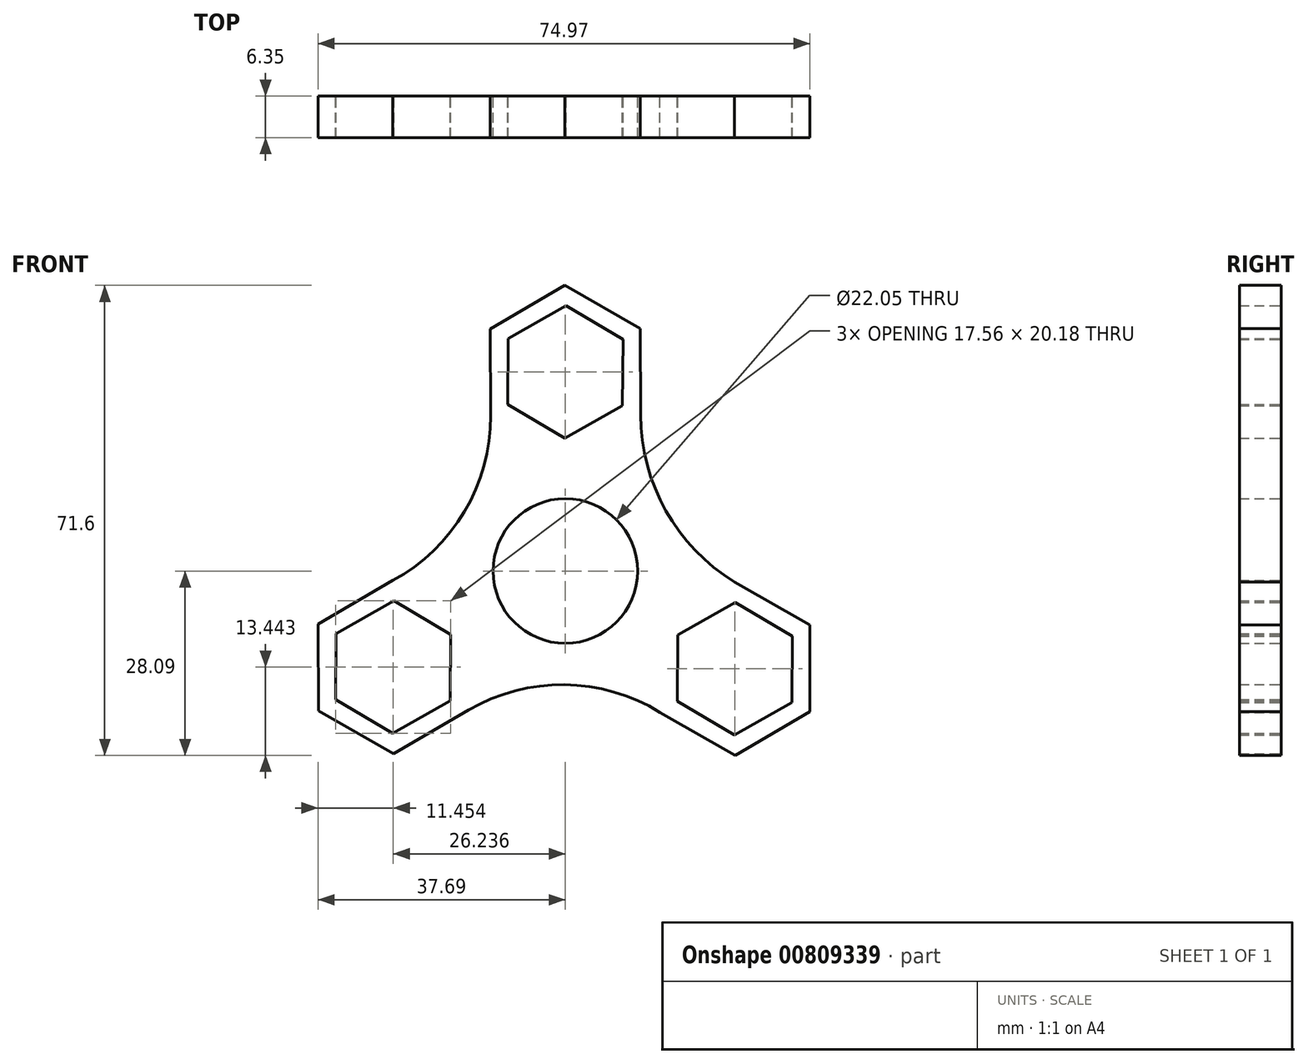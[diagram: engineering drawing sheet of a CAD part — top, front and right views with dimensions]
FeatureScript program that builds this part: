
annotation { "Feature Type Name" : "Feature", "Feature Type Description" : "" }
export const myFeature = defineFeature(function(context is Context, id is Id, definition is map)
    precondition{}
    {
        {
            var Q0;
            Q0=qCreatedBy(makeId("Front.planeOp"),FACE);
            var sketch = newSketch(context, id + "F0", { "sketchPlane" : qUnion([Q0])});
            skCircle(sketch, "E0", {"center": v(0, 0) * mm, "radius": 14.29 * mm});
            skCircle(sketch, "E1", {"center": v(0, 0) * mm, "radius": 11.02 * mm});
            skCircle(sketch, "E2.cCircle", {"center": v(0, 30.31) * mm, "radius": 11.43 * mm, "construction": true});
            skLineSegment(sketch, "E2.0", {"start": v(-0.05, 43.51) * mm, "end": v(11.4, 36.96) * mm});
            skLineSegment(sketch, "E2.1", {"start": v(11.4, 36.96) * mm, "end": v(11.46, 23.76) * mm});
            skLineSegment(sketch, "E2.2", {"start": v(11.46, 23.76) * mm, "end": v(0.05, 17.12) * mm});
            skLineSegment(sketch, "E2.3", {"start": v(0.05, 17.12) * mm, "end": v(-11.4, 23.67) * mm});
            skLineSegment(sketch, "E2.4", {"start": v(-11.4, 23.67) * mm, "end": v(-11.46, 36.87) * mm});
            skLineSegment(sketch, "E2.5", {"start": v(-11.46, 36.87) * mm, "end": v(-0.05, 43.51) * mm});
            skPoint(sketch, "E2.0.midPoint", {"position": v(5.67, 40.24) * mm});
            skCircle(sketch, "E3.cCircle", {"center": v(0, 30.31) * mm, "radius": 8.74 * mm, "construction": true});
            skLineSegment(sketch, "E3.0", {"start": v(0.09, 40.4) * mm, "end": v(8.78, 35.28) * mm});
            skLineSegment(sketch, "E3.1", {"start": v(8.78, 35.28) * mm, "end": v(8.7, 25.2) * mm});
            skLineSegment(sketch, "E3.2", {"start": v(8.7, 25.2) * mm, "end": v(-0.09, 20.22) * mm});
            skLineSegment(sketch, "E3.3", {"start": v(-0.09, 20.22) * mm, "end": v(-8.78, 25.35) * mm});
            skLineSegment(sketch, "E3.4", {"start": v(-8.78, 25.35) * mm, "end": v(-8.7, 35.44) * mm});
            skLineSegment(sketch, "E3.5", {"start": v(-8.7, 35.44) * mm, "end": v(0.09, 40.4) * mm});
            skPoint(sketch, "E3.0.midPoint", {"position": v(4.44, 37.84) * mm});
            skLineSegment(sketch, "E4.1.0", {"start": v(-14.83, -8) * mm, "end": v(-14.78, -21.2) * mm});
            skLineSegment(sketch, "E4.1.1", {"start": v(-26.29, -1.45) * mm, "end": v(-14.83, -8) * mm});
            skLineSegment(sketch, "E4.1.2", {"start": v(-14.78, -21.2) * mm, "end": v(-26.18, -27.84) * mm});
            skPoint(sketch, "E4.1.3", {"position": v(-34.97, -14.57) * mm});
            skLineSegment(sketch, "E4.1.4", {"start": v(-26.18, -27.84) * mm, "end": v(-37.64, -21.3) * mm});
            skLineSegment(sketch, "E4.1.5", {"start": v(-37.7, -8.1) * mm, "end": v(-26.29, -1.45) * mm});
            skLineSegment(sketch, "E4.1.6", {"start": v(-17.54, -19.77) * mm, "end": v(-26.33, -24.74) * mm});
            skLineSegment(sketch, "E4.1.7", {"start": v(-26.33, -24.74) * mm, "end": v(-35.02, -19.61) * mm});
            skPoint(sketch, "E4.1.9", {"position": v(-37.67, -14.7) * mm});
            skLineSegment(sketch, "E4.1.10", {"start": v(-26.15, -4.56) * mm, "end": v(-17.45, -9.68) * mm});
            skCircle(sketch, "E4.1.12", {"center": v(-26.24, -14.65) * mm, "radius": 8.74 * mm, "construction": true});
            skLineSegment(sketch, "E4.1.13", {"start": v(-37.64, -21.3) * mm, "end": v(-37.7, -8.1) * mm});
            skCircle(sketch, "E4.1.14", {"center": v(-26.24, -14.65) * mm, "radius": 11.43 * mm, "construction": true});
            skLineSegment(sketch, "E4.1.15", {"start": v(-17.45, -9.68) * mm, "end": v(-17.54, -19.77) * mm});
            skLineSegment(sketch, "E4.1.16", {"start": v(-34.93, -9.52) * mm, "end": v(-26.15, -4.56) * mm});
            skLineSegment(sketch, "E4.1.17", {"start": v(-35.02, -19.61) * mm, "end": v(-34.93, -9.52) * mm});
            skLineSegment(sketch, "E4.2.0", {"start": v(14.36, -8.34) * mm, "end": v(25.76, -1.69) * mm});
            skLineSegment(sketch, "E4.2.1", {"start": v(14.42, -21.53) * mm, "end": v(14.36, -8.34) * mm});
            skLineSegment(sketch, "E4.2.2", {"start": v(25.76, -1.69) * mm, "end": v(37.22, -8.24) * mm});
            skPoint(sketch, "E4.2.3", {"position": v(30.12, -22.5) * mm});
            skLineSegment(sketch, "E4.2.4", {"start": v(37.22, -8.24) * mm, "end": v(37.28, -21.44) * mm});
            skLineSegment(sketch, "E4.2.5", {"start": v(25.87, -28.09) * mm, "end": v(14.42, -21.53) * mm});
            skLineSegment(sketch, "E4.2.6", {"start": v(25.9, -4.8) * mm, "end": v(34.6, -9.92) * mm});
            skLineSegment(sketch, "E4.2.7", {"start": v(34.6, -9.92) * mm, "end": v(34.51, -20) * mm});
            skPoint(sketch, "E4.2.9", {"position": v(31.57, -24.76) * mm});
            skLineSegment(sketch, "E4.2.10", {"start": v(17.04, -19.85) * mm, "end": v(17.13, -9.77) * mm});
            skCircle(sketch, "E4.2.12", {"center": v(25.82, -14.89) * mm, "radius": 8.74 * mm, "construction": true});
            skLineSegment(sketch, "E4.2.13", {"start": v(37.28, -21.44) * mm, "end": v(25.87, -28.09) * mm});
            skCircle(sketch, "E4.2.14", {"center": v(25.82, -14.89) * mm, "radius": 11.43 * mm, "construction": true});
            skLineSegment(sketch, "E4.2.15", {"start": v(17.13, -9.77) * mm, "end": v(25.9, -4.8) * mm});
            skLineSegment(sketch, "E4.2.16", {"start": v(25.73, -24.98) * mm, "end": v(17.04, -19.85) * mm});
            skLineSegment(sketch, "E4.2.17", {"start": v(34.51, -20) * mm, "end": v(25.73, -24.98) * mm});
            skPoint(sketch, "E4.center", {"position": v(-0.14, 0.26) * mm});
            skArc(sketch, "E5", {"start": v(-26.29, -1.45) * mm, "mid": v(-15.38, 9.05) * mm, "end": v(-11.4, 23.67) * mm});
            skArc(sketch, "E6", {"start": v(14.42, -21.53) * mm, "mid": v(-0.14, -17.33) * mm, "end": v(-14.78, -21.2) * mm});
            skArc(sketch, "E7", {"start": v(11.46, 23.76) * mm, "mid": v(15.3, 9.18) * mm, "end": v(25.76, -1.69) * mm});
            skSolve(sketch);
        }
        {
            var Q0;
            Q0=makeQuery(id+"F0.imprint","IMPRINT",FACE,{"disambiguationData":[TD([[makeQuery(id+"F0.imprint","IMPRINT",EDGE,{"derivedFrom":sQuery(id+"F0.wireOp",EDGE,"E2.0")}),-1.0]])]});
            var Q1;
            {var subQ5=sQuery(id+"F0.wireOp",EDGE,"E4.1.8");var subQ6=sQuery(id+"F0.wireOp",EDGE,"E0");var subQ7=makeQuery(id+"F0.imprint","INTERSECT",VERTEX,{"disambiguationData":[OD(0.0)],"derivedFrom":[subQ6,subQ5]});Q1=makeQuery(id+"F0.imprint","IMPRINT",FACE,{"disambiguationData":[TD([[makeQuery(id+"F0.imprint","IMPRINT",EDGE,{"disambiguationData":[TD([[subQ7,1.0]])],"derivedFrom":subQ6}),1.0]])]});}
            var Q2;
            Q2=makeQuery(id+"F0.imprint","IMPRINT",FACE,{"disambiguationData":[TD([[makeQuery(id+"F0.imprint","IMPRINT",EDGE,{"derivedFrom":sQuery(id+"F0.wireOp",EDGE,"E4.1.0")}),-1.0]])]});
            var Q3;
            Q3=makeQuery(id+"F0.imprint","IMPRINT",FACE,{"disambiguationData":[TD([[makeQuery(id+"F0.imprint","IMPRINT",EDGE,{"derivedFrom":sQuery(id+"F0.wireOp",EDGE,"E4.2.0")}),-1.0]])]});
            var Q4;
            Q4=makeQuery(id+"F0.imprint","IMPRINT",FACE,{"disambiguationData":[TD([[makeQuery(id+"F0.imprint","IMPRINT",EDGE,{"derivedFrom":sQuery(id+"F0.wireOp",EDGE,"E2.2")}),1.0]])]});
            var Q5;
            {var subQ0=sQuery(id+"F0.wireOp",EDGE,"E4.2.8");var subQ1=sQuery(id+"F0.wireOp",EDGE,"E0");var subQ2=makeQuery(id+"F0.imprint","INTERSECT",VERTEX,{"disambiguationData":[OD(0.0)],"derivedFrom":[subQ1,subQ0]});Q5=makeQuery(id+"F0.imprint","IMPRINT",FACE,{"disambiguationData":[TD([[makeQuery(id+"F0.imprint","IMPRINT",EDGE,{"disambiguationData":[TD([[subQ2,1.0]])],"derivedFrom":subQ1}),-1.0]])]});}
            extrude(context, id + "F1", {"entities" : qUnion([Q0, Q1, Q2, Q3, Q4, Q5]), "depth" : 6.35 * mm, "offsetDistance" : 25.4 * mm});
        }
    });
